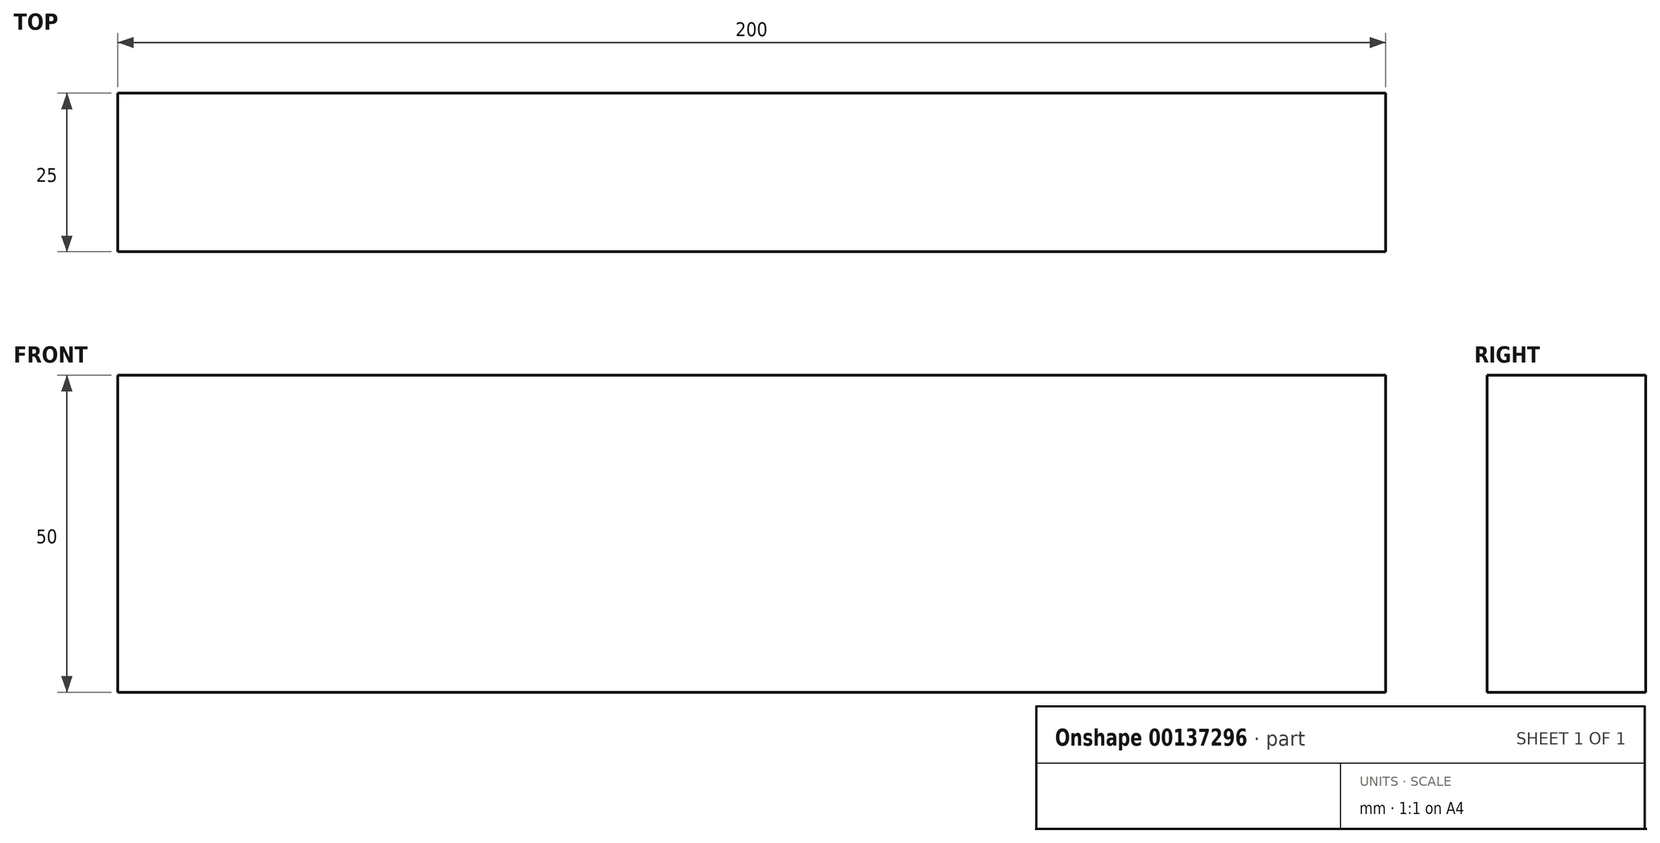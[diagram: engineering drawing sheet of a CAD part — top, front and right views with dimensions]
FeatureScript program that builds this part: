
annotation { "Feature Type Name" : "Feature", "Feature Type Description" : "" }
export const myFeature = defineFeature(function(context is Context, id is Id, definition is map)
    precondition{}
    {
        {
            var Q0;
            Q0=qCreatedBy(makeId("Front.planeOp"),FACE);
            var sketch = newSketch(context, id + "F0", { "sketchPlane" : qUnion([Q0])});
            skLineSegment(sketch, "E0.bottom", {"start": v(-125.96, 43.53) * mm, "end": v(74.04, 43.53) * mm});
            skLineSegment(sketch, "E0.top", {"start": v(-125.96, -6.47) * mm, "end": v(74.04, -6.47) * mm});
            skLineSegment(sketch, "E0.left", {"start": v(-125.96, 43.53) * mm, "end": v(-125.96, -6.47) * mm});
            skLineSegment(sketch, "E0.right", {"start": v(74.04, 43.53) * mm, "end": v(74.04, -6.47) * mm});
            skLineSegment(sketch, "E1.bottom", {"start": v(-34.37, 73.28) * mm, "end": v(8.62, 73.28) * mm});
            skLineSegment(sketch, "E1.top", {"start": v(-34.37, 67.68) * mm, "end": v(8.62, 67.68) * mm});
            skLineSegment(sketch, "E1.left", {"start": v(-34.37, 73.28) * mm, "end": v(-34.37, 67.68) * mm});
            skLineSegment(sketch, "E1.right", {"start": v(8.62, 73.28) * mm, "end": v(8.62, 67.68) * mm});
            skSolve(sketch);
        }
        {
            var Q0;
            Q0=makeQuery(id+"F0.imprint","IMPRINT",FACE,{"disambiguationData":[TD([[makeQuery(id+"F0.imprint","IMPRINT",EDGE,{"derivedFrom":sQuery(id+"F0.wireOp",EDGE,"E0.bottom")}),-1.0]])]});
            extrude(context, id + "F1", {"entities" : qUnion([Q0]), "depth" : 25 * mm});
        }
    });
